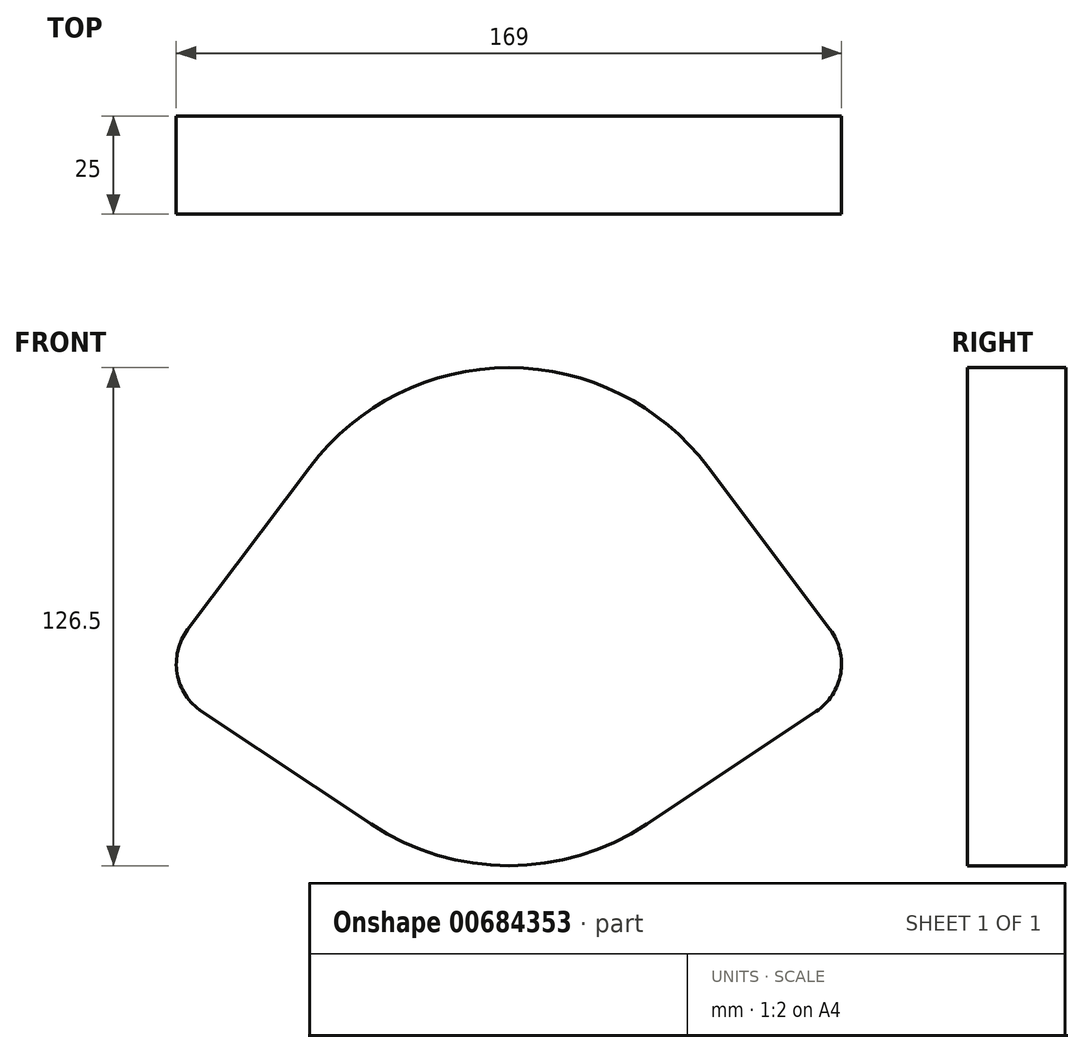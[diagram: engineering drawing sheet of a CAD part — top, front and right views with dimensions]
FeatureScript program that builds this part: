
annotation { "Feature Type Name" : "Feature", "Feature Type Description" : "" }
export const myFeature = defineFeature(function(context is Context, id is Id, definition is map)
    precondition{}
    {
        {
            var Q0;
            Q0=qCreatedBy(makeId("Front.planeOp"),FACE);
            var sketch = newSketch(context, id + "F0", { "sketchPlane" : qUnion([Q0])});
            skArc(sketch, "E0", {"start": v(-35.02, -52.67) * mm, "mid": v(0, -63.25) * mm, "end": v(35.02, -52.67) * mm});
            skArc(sketch, "E1", {"start": v(-81.6, -3.29) * mm, "mid": v(-84.3, -14.45) * mm, "end": v(-78.03, -24.07) * mm});
            skArc(sketch, "E2.MirrorC", {"start": v(81.6, -3.29) * mm, "mid": v(84.3, -14.45) * mm, "end": v(78.03, -24.07) * mm});
            skLineSegment(sketch, "E3", {"start": v(-35.02, -52.67) * mm, "end": v(-78.03, -24.07) * mm});
            skLineSegment(sketch, "E4", {"start": v(-81.6, -3.29) * mm, "end": v(-50.56, 38) * mm});
            skLineSegment(sketch, "E5", {"start": v(50.56, 38) * mm, "end": v(81.6, -3.29) * mm});
            skLineSegment(sketch, "E6", {"start": v(78.03, -24.07) * mm, "end": v(35.02, -52.67) * mm});
            skArc(sketch, "E7.trimOffspring", {"start": v(50.56, 38) * mm, "mid": v(0, 63.25) * mm, "end": v(-50.56, 38) * mm});
            skSolve(sketch);
        }
        {
            var Q0;
            Q0=makeQuery(id+"F0.imprint","IMPRINT",FACE,{"disambiguationData":[TD([[makeQuery(id+"F0.imprint","IMPRINT",EDGE,{"derivedFrom":sQuery(id+"F0.wireOp",EDGE,"E0")}),1.0]])]});
            extrude(context, id + "F1", {"entities" : qUnion([Q0]), "depth" : 25 * mm, "offsetDistance" : 25 * mm});
        }
    });
